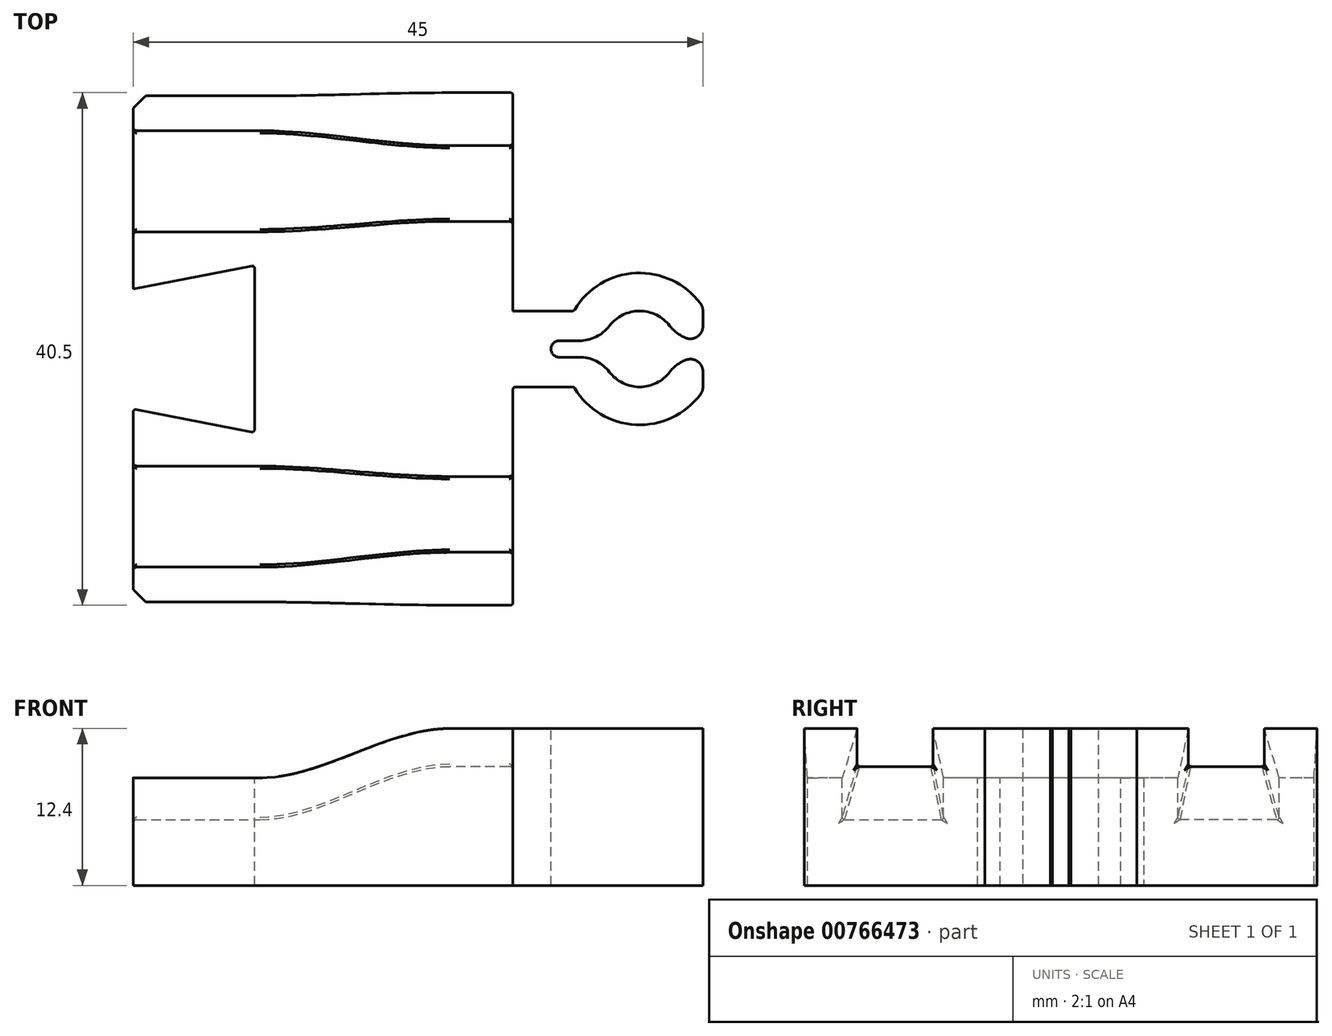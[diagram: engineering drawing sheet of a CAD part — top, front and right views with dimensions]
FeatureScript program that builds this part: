
annotation { "Feature Type Name" : "Feature", "Feature Type Description" : "" }
export const myFeature = defineFeature(function(context is Context, id is Id, definition is map)
    precondition{}
    {
        {
            var Q0;
            Q0=qCreatedBy(makeId("Right.planeOp"),FACE);
            cPlane(context, id + "F0", {"entities" : qUnion([Q0]), "cplaneType" : CPlaneType.OFFSET, "offset" : 15 * mm, "width" : 150 * mm, "height" : 150 * mm});
        }
        {
            var Q0;
            Q0=qCreatedBy(makeId("Right.planeOp"),FACE);
            var sketch = newSketch(context, id + "F1", { "sketchPlane" : qUnion([Q0])});
            skLineSegment(sketch, "E0.bottom", {"start": v(20, 0) * mm, "end": v(-20, 0) * mm});
            skLineSegment(sketch, "E0.top", {"start": v(20, 8.5) * mm, "end": v(17.25, 8.5) * mm});
            skLineSegment(sketch, "E0.left", {"start": v(20, 0) * mm, "end": v(20, 8.5) * mm});
            skLineSegment(sketch, "E0.right", {"start": v(-20, 0) * mm, "end": v(-20, 8.5) * mm});
            skPoint(sketch, "E0.middle", {"position": v(0, 4.25) * mm});
            skLineSegment(sketch, "E1.bottom", {"start": v(17.25, 5.2) * mm, "end": v(9.25, 5.2) * mm});
            skLineSegment(sketch, "E1.left", {"start": v(17.25, 5.2) * mm, "end": v(17.25, 8.5) * mm});
            skLineSegment(sketch, "E1.right", {"start": v(9.25, 5.2) * mm, "end": v(9.25, 8.5) * mm});
            skPoint(sketch, "E1.middle", {"position": v(13.25, 12.03) * mm});
            skPoint(sketch, "E2.orphan", {"position": v(9.25, 18.86) * mm});
            skPoint(sketch, "E3.orphan", {"position": v(17.25, 18.86) * mm});
            skLineSegment(sketch, "E4.trimOffspring", {"start": v(9.25, 8.5) * mm, "end": v(-9.25, 8.5) * mm});
            skLineSegment(sketch, "E5.MirrorCS", {"start": v(-9.25, 5.2) * mm, "end": v(-9.25, 8.5) * mm});
            skLineSegment(sketch, "E6.MirrorCS", {"start": v(-17.25, 5.2) * mm, "end": v(-9.25, 5.2) * mm});
            skLineSegment(sketch, "E7.MirrorCS", {"start": v(-17.25, 5.2) * mm, "end": v(-17.25, 8.5) * mm});
            skLineSegment(sketch, "E8.trimOffspring", {"start": v(-17.25, 8.5) * mm, "end": v(-20, 8.5) * mm});
            skSolve(sketch);
        }
        {
            var Q0;
            Q0=makeQuery(id+"F1.imprint","IMPRINT",FACE,{"disambiguationData":[TD([[makeQuery(id+"F1.imprint","IMPRINT",EDGE,{"derivedFrom":sQuery(id+"F1.wireOp",EDGE,"E0.bottom")}),-1.0]])]});
            extrude(context, id + "F2", {"entities" : qUnion([Q0]), "oppositeDirection" : true, "depth" : 10 * mm, "offsetDistance" : 25 * mm});
        }
        {
            var Q0;
            Q0=qCreatedBy(id+"F0.planeOp",FACE);
            var sketch = newSketch(context, id + "F3", { "sketchPlane" : qUnion([Q0])});
            skLineSegment(sketch, "E9.bottom", {"start": v(20.25, 0) * mm, "end": v(-20.25, 0) * mm});
            skLineSegment(sketch, "E9.top", {"start": v(20.25, 12.4) * mm, "end": v(16.07, 12.4) * mm});
            skLineSegment(sketch, "E9.left", {"start": v(20.25, 0) * mm, "end": v(20.25, 12.4) * mm});
            skLineSegment(sketch, "E9.right", {"start": v(-20.25, 0) * mm, "end": v(-20.25, 12.4) * mm});
            skPoint(sketch, "E9.middle", {"position": v(0, 6.2) * mm});
            skLineSegment(sketch, "E10.bottom", {"start": v(16.07, 9.4) * mm, "end": v(10.07, 9.4) * mm});
            skLineSegment(sketch, "E10.left", {"start": v(16.07, 9.4) * mm, "end": v(16.07, 12.4) * mm});
            skLineSegment(sketch, "E10.right", {"start": v(10.07, 9.4) * mm, "end": v(10.07, 12.4) * mm});
            skPoint(sketch, "E10.middle", {"position": v(13.07, 12.4) * mm});
            skPoint(sketch, "E11.orphan", {"position": v(10.07, 15.41) * mm});
            skLineSegment(sketch, "E12.trimOffspring", {"start": v(10.08, 12.4) * mm, "end": v(-10.08, 12.4) * mm});
            skPoint(sketch, "E13.orphan", {"position": v(16.07, 15.41) * mm});
            skLineSegment(sketch, "E14.MirrorCS", {"start": v(-10.08, 9.4) * mm, "end": v(-10.08, 12.4) * mm});
            skLineSegment(sketch, "E15.MirrorCS", {"start": v(-16.07, 9.4) * mm, "end": v(-10.07, 9.4) * mm});
            skLineSegment(sketch, "E16.MirrorCS", {"start": v(-16.07, 9.4) * mm, "end": v(-16.07, 12.4) * mm});
            skLineSegment(sketch, "E17.trimOffspring", {"start": v(-16.07, 12.4) * mm, "end": v(-20.25, 12.4) * mm});
            skSolve(sketch);
        }
        {
            var Q0;
            Q0=qSketchRegion(id+"F3",true);
            extrude(context, id + "F4", {"entities" : qUnion([Q0]), "depth" : 5 * mm, "offsetDistance" : 25 * mm});
        }
        {
            var Q0;
            Q0=makeQuery(id+"F4.opExtrude","CAP_FACE",FACE,{"disambiguationData":[OSD([sQuery(id+"F3.wireOp",EDGE,"E9.bottom"),sQuery(id+"F3.wireOp",EDGE,"E9.top"),sQuery(id+"F3.wireOp",EDGE,"E9.left"),sQuery(id+"F3.wireOp",EDGE,"E9.right"),sQuery(id+"F3.wireOp",EDGE,"E10.bottom"),sQuery(id+"F3.wireOp",EDGE,"E10.left"),sQuery(id+"F3.wireOp",EDGE,"E10.right"),sQuery(id+"F3.wireOp",EDGE,"E12.trimOffspring"),sQuery(id+"F3.wireOp",EDGE,"E14.MirrorCS"),sQuery(id+"F3.wireOp",EDGE,"E15.MirrorCS"),sQuery(id+"F3.wireOp",EDGE,"E16.MirrorCS"),sQuery(id+"F3.wireOp",EDGE,"E17.trimOffspring")])],"isStart":true});
            var Q1;
            Q1=makeQuery(id+"F2.opExtrude","CAP_FACE",FACE,{"disambiguationData":[OSD([sQuery(id+"F1.wireOp",EDGE,"E0.bottom"),sQuery(id+"F1.wireOp",EDGE,"E0.top"),sQuery(id+"F1.wireOp",EDGE,"E0.left"),sQuery(id+"F1.wireOp",EDGE,"E0.right"),sQuery(id+"F1.wireOp",EDGE,"E1.bottom"),sQuery(id+"F1.wireOp",EDGE,"E1.left"),sQuery(id+"F1.wireOp",EDGE,"E1.right"),sQuery(id+"F1.wireOp",EDGE,"E4.trimOffspring"),sQuery(id+"F1.wireOp",EDGE,"E5.MirrorCS"),sQuery(id+"F1.wireOp",EDGE,"E6.MirrorCS"),sQuery(id+"F1.wireOp",EDGE,"E7.MirrorCS"),sQuery(id+"F1.wireOp",EDGE,"E8.trimOffspring")])],"isStart":true});
            loft(context, id + "F5", {"operationType" : NewBodyOperationType.ADD, "startCondition" : LoftEndDerivativeType.NORMAL_TO_PROFILE, "startMagnitude" : 1, "endCondition" : LoftEndDerivativeType.NORMAL_TO_PROFILE, "endMagnitude" : 1, "sheetProfilesArray" : [{ "sheetProfileEntities" : qUnion([Q0]) }, { "sheetProfileEntities" : qUnion([Q1]) }]});
        }
        {
            var Q0;
            Q0=makeQuery(id+"F2.opExtrude","SWEPT_FACE",FACE,{"disambiguationData":[OSD([sQuery(id+"F1.wireOp",EDGE,"E4.trimOffspring")])]});
            var sketch = newSketch(context, id + "F6", { "sketchPlane" : qUnion([Q0])});
            skLineSegment(sketch, "E18.0", {"start": v(-10, 4.75) * mm, "end": v(-10, -4.75) * mm});
            skLineSegment(sketch, "E19", {"start": v(-10, 4.75) * mm, "end": v(-0.4, 6.6) * mm});
            skLineSegment(sketch, "E20", {"start": v(-0.4, 0) * mm, "end": v(-10, 0) * mm, "construction": true});
            skLineSegment(sketch, "E21.MirrorCS", {"start": v(-10, -4.75) * mm, "end": v(-0.4, -6.6) * mm});
            skLineSegment(sketch, "E22", {"start": v(-0.4, 6.6) * mm, "end": v(-0.4, -6.6) * mm});
            skPoint(sketch, "E23.orphan", {"position": v(-10, 9.25) * mm});
            skPoint(sketch, "E24.orphan", {"position": v(-10, -9.25) * mm});
            skPoint(sketch, "E25.orphan", {"position": v(-32.28, -1.5) * mm});
            skSolve(sketch);
        }
        {
            var Q0;
            Q0=makeQuery(id+"F4.opExtrude","SWEPT_FACE",FACE,{"disambiguationData":[OSD([sQuery(id+"F3.wireOp",EDGE,"E12.trimOffspring")])]});
            var sketch = newSketch(context, id + "F7", { "sketchPlane" : qUnion([Q0])});
            skLineSegment(sketch, "E26.0", {"start": v(20, 10.07) * mm, "end": v(20, -10.08) * mm, "construction": true});
            skLineSegment(sketch, "E27.bottom", {"start": v(20, 3) * mm, "end": v(24.8, 3) * mm});
            skLineSegment(sketch, "E27.top", {"start": v(20, -3) * mm, "end": v(24.8, -3) * mm});
            skLineSegment(sketch, "E27.left", {"start": v(20, 3) * mm, "end": v(20, -3) * mm});
            skPoint(sketch, "E27.middle", {"position": v(23.65, 0) * mm});
            skPoint(sketch, "E27.middle.positionSnap0", {"position": v(20, 0) * mm});
            skPoint(sketch, "E27.centerSnap0", {"position": v(20, 0) * mm});
            skArc(sketch, "E28", {"start": v(35, 3.32) * mm, "mid": v(29.81, 6) * mm, "end": v(24.8, 3) * mm});
            skLineSegment(sketch, "E29", {"start": v(35, 3.32) * mm, "end": v(35, 0.65) * mm});
            skPoint(sketch, "E30.orphan", {"position": v(27.3, 3) * mm});
            skPoint(sketch, "E31.orphan", {"position": v(27.3, -3) * mm});
            skArc(sketch, "E32.trimOffspring", {"start": v(24.8, -3) * mm, "mid": v(29.81, -6) * mm, "end": v(35, -3.32) * mm});
            skLineSegment(sketch, "E33.bottom", {"start": v(23.65, 0.65) * mm, "end": v(27.07, 0.65) * mm});
            skLineSegment(sketch, "E33.top", {"start": v(23.65, -0.65) * mm, "end": v(27.07, -0.65) * mm});
            skArc(sketch, "E34", {"start": v(23.65, 0.65) * mm, "mid": v(23, 0) * mm, "end": v(23.65, -0.65) * mm});
            skPoint(sketch, "E33.left.start.orphan", {"position": v(25, 0.65) * mm});
            skPoint(sketch, "E35.orphan", {"position": v(25, -0.65) * mm});
            skLineSegment(sketch, "E36.trimOffspring", {"start": v(35, -0.65) * mm, "end": v(35, -3.46) * mm});
            skPoint(sketch, "E33.right.end.orphan", {"position": v(35, -0.65) * mm});
            skPoint(sketch, "E33.right.start.orphan", {"position": v(35, 0.65) * mm});
            skArc(sketch, "E37", {"start": v(32.93, 0.65) * mm, "mid": v(30, 3) * mm, "end": v(27.07, 0.65) * mm});
            skLineSegment(sketch, "E38.trimOffspring", {"start": v(32.93, -0.65) * mm, "end": v(35, -0.65) * mm});
            skLineSegment(sketch, "E39.trimOffspring", {"start": v(32.93, 0.65) * mm, "end": v(35, 0.65) * mm});
            skArc(sketch, "E40.trimOffspring", {"start": v(27.07, -0.65) * mm, "mid": v(30, -3) * mm, "end": v(32.93, -0.65) * mm});
            skSolve(sketch);
        }
        {
            var Q0;
            Q0=makeQuery(id+"F7.imprint","IMPRINT",FACE,{"disambiguationData":[TD([[makeQuery(id+"F7.imprint","IMPRINT",EDGE,{"derivedFrom":sQuery(id+"F7.wireOp",EDGE,"E27.bottom")}),-1.0]])]});
            var Q1;
            {var subQ0=sQuery(id+"F3.wireOp",EDGE,"E9.right");var subQ1=sQuery(id+"F3.wireOp",EDGE,"E9.left");var subQ2=sQuery(id+"F3.wireOp",EDGE,"E9.bottom");var subQ3=sQuery(id+"F1.wireOp",EDGE,"E0.right");var subQ4=sQuery(id+"F1.wireOp",EDGE,"E0.left");var subQ5=sQuery(id+"F1.wireOp",EDGE,"E0.bottom");Q1=makeQuery(id+"FUpJ5mfuHsCIaRH_1.boolean.opBoolean","MERGE",FACE,{"derivedFrom":[makeQuery(id+"F5.boolean.opBoolean","MERGE",FACE,{"derivedFrom":[makeQuery(id+"F2.opExtrude","SWEPT_FACE",FACE,{"disambiguationData":[OSD([subQ5])]}),makeQuery(id+"F4.opExtrude","SWEPT_FACE",FACE,{"disambiguationData":[OSD([subQ2])]}),makeQuery(id+"F5.opLoft","SWEPT_FACE",FACE,{"disambiguationData":[OSD([subQ5,subQ4,subQ3,subQ2,subQ1,subQ0])]})]}),makeQuery(id+"FUpJ5mfuHsCIaRH_1.opExtrude","CAP_FACE",FACE,{"disambiguationData":[OSD([subQ5,subQ4,subQ3,subQ2,subQ1,subQ0])],"isStart":false})]});}
            extrude(context, id + "F8", {"entities" : qUnion([Q0]), "operationType" : NewBodyOperationType.ADD, "endBound" : BoundingType.UP_TO_SURFACE, "oppositeDirection" : true, "depth" : 25 * mm, "endBoundEntityFace" : qUnion([Q1]), "offsetDistance" : 25 * mm});
        }
        {
            var Q0;
            Q0=makeQuery(id+"F8.opExtrude","SWEPT_EDGE",EDGE,{"disambiguationData":[OSD([sQuery(id+"F7.wireOp",EDGE,"E33.bottom"),sQuery(id+"F7.wireOp",EDGE,"E37")])]});
            var Q1;
            Q1=makeQuery(id+"F8.opExtrude","SWEPT_EDGE",EDGE,{"disambiguationData":[OSD([sQuery(id+"F7.wireOp",EDGE,"E33.top"),sQuery(id+"F7.wireOp",EDGE,"E40.trimOffspring")])]});
            var Q2;
            Q2=makeQuery(id+"F8.opExtrude","SWEPT_EDGE",EDGE,{"disambiguationData":[OSD([sQuery(id+"F7.wireOp",EDGE,"E37"),sQuery(id+"F7.wireOp",EDGE,"E39.trimOffspring")])]});
            var Q3;
            Q3=makeQuery(id+"F8.opExtrude","SWEPT_EDGE",EDGE,{"disambiguationData":[OSD([sQuery(id+"F7.wireOp",EDGE,"E38.trimOffspring"),sQuery(id+"F7.wireOp",EDGE,"E40.trimOffspring")])]});
            fillet(context, id + "F9", {"entities" : qUnion([Q0, Q1, Q2, Q3]), "radius" : 3 * mm, "tangentPropagation" : true, "allowEdgeOverflow" : false});
        }
        {
            var Q0;
            Q0=makeQuery(id+"F8.opExtrude","SWEPT_EDGE",EDGE,{"disambiguationData":[OSD([sQuery(id+"F7.wireOp",EDGE,"E28"),sQuery(id+"F7.wireOp",EDGE,"E29")])]});
            var Q1;
            Q1=makeQuery(id+"F8.opExtrude","SWEPT_EDGE",EDGE,{"disambiguationData":[OSD([sQuery(id+"F7.wireOp",EDGE,"E29"),sQuery(id+"F7.wireOp",EDGE,"E39.trimOffspring")])]});
            var Q2;
            Q2=makeQuery(id+"F8.opExtrude","SWEPT_EDGE",EDGE,{"disambiguationData":[OSD([sQuery(id+"F7.wireOp",EDGE,"E36.trimOffspring"),sQuery(id+"F7.wireOp",EDGE,"E38.trimOffspring")])]});
            var Q3;
            Q3=makeQuery(id+"F8.opExtrude","SWEPT_EDGE",EDGE,{"disambiguationData":[OSD([sQuery(id+"F7.wireOp",EDGE,"E32.trimOffspring"),sQuery(id+"F7.wireOp",EDGE,"E36.trimOffspring")])]});
            fillet(context, id + "F10", {"entities" : qUnion([Q0, Q1, Q2, Q3]), "radius" : 1 * mm, "tangentPropagation" : true, "allowEdgeOverflow" : false});
        }
        {
            var Q0;
            Q0=makeQuery(id+"F8.opExtrude","SWEPT_EDGE",EDGE,{"disambiguationData":[OSD([sQuery(id+"F3.wireOp",EDGE,"E12.trimOffspring"),sQuery(id+"F7.wireOp",EDGE,"E27.top"),sQuery(id+"F7.wireOp",EDGE,"E27.left")])]});
            var Q1;
            Q1=makeQuery(id+"F8.opExtrude","SWEPT_EDGE",EDGE,{"disambiguationData":[OSD([sQuery(id+"F7.wireOp",EDGE,"E27.top"),sQuery(id+"F7.wireOp",EDGE,"E32.trimOffspring")])]});
            var Q2;
            Q2=makeQuery(id+"F8.opExtrude","SWEPT_EDGE",EDGE,{"disambiguationData":[OSD([sQuery(id+"F3.wireOp",EDGE,"E12.trimOffspring"),sQuery(id+"F7.wireOp",EDGE,"E27.bottom"),sQuery(id+"F7.wireOp",EDGE,"E27.left")])]});
            var Q3;
            Q3=makeQuery(id+"F8.opExtrude","SWEPT_EDGE",EDGE,{"disambiguationData":[OSD([sQuery(id+"F7.wireOp",EDGE,"E27.bottom"),sQuery(id+"F7.wireOp",EDGE,"E28")])]});
            fillet(context, id + "F11", {"entities" : qUnion([Q0, Q1, Q2, Q3]), "radius" : 0.2 * mm, "tangentPropagation" : true, "allowEdgeOverflow" : false});
        }
        {
            var Q0;
            Q0=makeQuery(id+"F2.opExtrude","CAP_EDGE",EDGE,{"disambiguationData":[OSD([sQuery(id+"F1.wireOp",EDGE,"E1.left")])],"isStart":false});
            var Q1;
            Q1=makeQuery(id+"F2.opExtrude","CAP_EDGE",EDGE,{"disambiguationData":[OSD([sQuery(id+"F1.wireOp",EDGE,"E1.right")])],"isStart":false});
            var Q2;
            Q2=makeQuery(id+"F2.opExtrude","CAP_EDGE",EDGE,{"disambiguationData":[OSD([sQuery(id+"F1.wireOp",EDGE,"E1.bottom")])],"isStart":false});
            var Q3;
            Q3=makeQuery(id+"F2.opExtrude","CAP_EDGE",EDGE,{"disambiguationData":[OSD([sQuery(id+"F1.wireOp",EDGE,"E5.MirrorCS")])],"isStart":false});
            var Q4;
            Q4=makeQuery(id+"F2.opExtrude","CAP_EDGE",EDGE,{"disambiguationData":[OSD([sQuery(id+"F1.wireOp",EDGE,"E6.MirrorCS")])],"isStart":false});
            var Q5;
            Q5=makeQuery(id+"F2.opExtrude","CAP_EDGE",EDGE,{"disambiguationData":[OSD([sQuery(id+"F1.wireOp",EDGE,"E7.MirrorCS")])],"isStart":false});
            var Q6;
            Q6=makeQuery(id+"F4.opExtrude","CAP_EDGE",EDGE,{"disambiguationData":[OSD([sQuery(id+"F3.wireOp",EDGE,"E16.MirrorCS")])],"isStart":false});
            var Q7;
            Q7=makeQuery(id+"F4.opExtrude","CAP_EDGE",EDGE,{"disambiguationData":[OSD([sQuery(id+"F3.wireOp",EDGE,"E15.MirrorCS")])],"isStart":false});
            var Q8;
            Q8=makeQuery(id+"F4.opExtrude","CAP_EDGE",EDGE,{"disambiguationData":[OSD([sQuery(id+"F3.wireOp",EDGE,"E14.MirrorCS")])],"isStart":false});
            var Q9;
            Q9=makeQuery(id+"F4.opExtrude","CAP_EDGE",EDGE,{"disambiguationData":[OSD([sQuery(id+"F3.wireOp",EDGE,"E10.left")])],"isStart":false});
            var Q10;
            Q10=makeQuery(id+"F4.opExtrude","CAP_EDGE",EDGE,{"disambiguationData":[OSD([sQuery(id+"F3.wireOp",EDGE,"E10.bottom")])],"isStart":false});
            var Q11;
            Q11=makeQuery(id+"F4.opExtrude","CAP_EDGE",EDGE,{"disambiguationData":[OSD([sQuery(id+"F3.wireOp",EDGE,"E10.right")])],"isStart":false});
            fillet(context, id + "F12", {"entities" : qUnion([Q0, Q1, Q2, Q3, Q4, Q5, Q6, Q7, Q8, Q9, Q10, Q11]), "radius" : 0.3 * mm, "tangentPropagation" : true, "allowEdgeOverflow" : false});
        }
        {
            var Q0;
            Q0=makeQuery(id+"F5.opLoft","SWEPT_EDGE",EDGE,{"disambiguationData":[OSD([sQuery(id+"F1.wireOp",EDGE,"E1.bottom"),sQuery(id+"F1.wireOp",EDGE,"E1.left"),sQuery(id+"F3.wireOp",EDGE,"E10.bottom"),sQuery(id+"F3.wireOp",EDGE,"E10.left")])]});
            var Q1;
            Q1=makeQuery(id+"F5.opLoft","SWEPT_EDGE",EDGE,{"disambiguationData":[OSD([sQuery(id+"F1.wireOp",EDGE,"E1.bottom"),sQuery(id+"F1.wireOp",EDGE,"E1.right"),sQuery(id+"F3.wireOp",EDGE,"E10.bottom"),sQuery(id+"F3.wireOp",EDGE,"E10.right")])]});
            var Q2;
            Q2=makeQuery(id+"F5.opLoft","SWEPT_EDGE",EDGE,{"disambiguationData":[OSD([sQuery(id+"F1.wireOp",EDGE,"E6.MirrorCS"),sQuery(id+"F1.wireOp",EDGE,"E7.MirrorCS"),sQuery(id+"F3.wireOp",EDGE,"E15.MirrorCS"),sQuery(id+"F3.wireOp",EDGE,"E16.MirrorCS")])]});
            var Q3;
            Q3=makeQuery(id+"F5.opLoft","SWEPT_EDGE",EDGE,{"disambiguationData":[OSD([sQuery(id+"F1.wireOp",EDGE,"E5.MirrorCS"),sQuery(id+"F1.wireOp",EDGE,"E6.MirrorCS"),sQuery(id+"F3.wireOp",EDGE,"E14.MirrorCS"),sQuery(id+"F3.wireOp",EDGE,"E15.MirrorCS")])]});
            fillet(context, id + "F13", {"entities" : qUnion([Q0, Q1, Q2, Q3]), "radius" : 0.2 * mm, "tangentPropagation" : true, "allowEdgeOverflow" : false});
        }
        {
            var Q0;
            Q0=makeQuery(id+"F6.imprint","IMPRINT",FACE,{"disambiguationData":[TD([[makeQuery(id+"F6.imprint","IMPRINT",EDGE,{"derivedFrom":sQuery(id+"F6.wireOp",EDGE,"E18.0")}),1.0]])]});
            extrude(context, id + "F14", {"entities" : qUnion([Q0]), "operationType" : NewBodyOperationType.REMOVE, "endBound" : BoundingType.UP_TO_NEXT, "oppositeDirection" : true, "depth" : 25 * mm, "offsetDistance" : 25 * mm});
        }
        {
            var Q0;
            Q0=makeQuery(id+"F14.boolean.opBoolean","COPY",EDGE,{"derivedFrom":makeQuery(id+"F14.opExtrude","SWEPT_EDGE",EDGE,{"disambiguationData":[OSD([sQuery(id+"F1.wireOp",EDGE,"E4.trimOffspring"),sQuery(id+"F6.wireOp",EDGE,"E18.0"),sQuery(id+"F6.wireOp",EDGE,"E19")])]})});
            var Q1;
            Q1=makeQuery(id+"F14.boolean.opBoolean","COPY",EDGE,{"derivedFrom":makeQuery(id+"F14.opExtrude","SWEPT_EDGE",EDGE,{"disambiguationData":[OSD([sQuery(id+"F1.wireOp",EDGE,"E4.trimOffspring"),sQuery(id+"F6.wireOp",EDGE,"E18.0"),sQuery(id+"F6.wireOp",EDGE,"E21.MirrorCS")])]})});
            var Q2;
            Q2=makeQuery(id+"F14.boolean.opBoolean","COPY",EDGE,{"derivedFrom":makeQuery(id+"F14.opExtrude","SWEPT_EDGE",EDGE,{"disambiguationData":[OSD([sQuery(id+"F6.wireOp",EDGE,"E19"),sQuery(id+"F6.wireOp",EDGE,"E22")])]})});
            var Q3;
            Q3=makeQuery(id+"F14.boolean.opBoolean","COPY",EDGE,{"derivedFrom":makeQuery(id+"F14.opExtrude","SWEPT_EDGE",EDGE,{"disambiguationData":[OSD([sQuery(id+"F6.wireOp",EDGE,"E21.MirrorCS"),sQuery(id+"F6.wireOp",EDGE,"E22")])]})});
            fillet(context, id + "F15", {"entities" : qUnion([Q0, Q1, Q2, Q3]), "radius" : 0.2 * mm, "tangentPropagation" : true, "allowEdgeOverflow" : false});
        }
        {
            var Q0;
            Q0=makeQuery(id+"F2.opExtrude","CAP_EDGE",EDGE,{"disambiguationData":[OSD([sQuery(id+"F1.wireOp",EDGE,"E0.left")])],"isStart":false});
            var Q1;
            Q1=makeQuery(id+"F2.opExtrude","CAP_EDGE",EDGE,{"disambiguationData":[OSD([sQuery(id+"F1.wireOp",EDGE,"E0.right")])],"isStart":false});
            chamfer(context, id + "F16", {"entities" : qUnion([Q0, Q1]), "width" : 1 * mm, "tangentPropagation" : true});
        }
        {
            var Q0;
            Q0=makeQuery(id+"F4.opExtrude","CAP_EDGE",EDGE,{"disambiguationData":[OSD([sQuery(id+"F3.wireOp",EDGE,"E9.left")])],"isStart":false});
            var Q1;
            {var subQ0=sQuery(id+"F1.wireOp",EDGE,"E0.left");Q1=makeQuery(id+"F16.opChamfer","BLEND_EDGE",EDGE,{"blendedFrom":[makeQuery(id+"F2.opExtrude","CAP_EDGE",EDGE,{"disambiguationData":[OSD([subQ0])],"isStart":false}),makeQuery(id+"F2.opExtrude","SWEPT_FACE",FACE,{"disambiguationData":[OSD([subQ0])]})],"blendedInto":[makeQuery(id+"F2.opExtrude","SWEPT_FACE",FACE,{"disambiguationData":[OSD([subQ0])]})]});}
            var Q2;
            {var subQ0=sQuery(id+"F1.wireOp",EDGE,"E7.MirrorCS");var subQ1=sQuery(id+"F1.wireOp",EDGE,"E5.MirrorCS");var subQ2=sQuery(id+"F1.wireOp",EDGE,"E0.bottom");var subQ6=sQuery(id+"F1.wireOp",EDGE,"E0.right");var subQ7=sQuery(id+"F1.wireOp",EDGE,"E0.left");var subQ8=sQuery(id+"F1.wireOp",EDGE,"E8.trimOffspring");var subQ9=sQuery(id+"F1.wireOp",EDGE,"E6.MirrorCS");var subQ10=sQuery(id+"F1.wireOp",EDGE,"E4.trimOffspring");Q2=makeQuery(id+"F16.opChamfer","BLEND_EDGE",EDGE,{"blendedFrom":[makeQuery(id+"F2.opExtrude","CAP_EDGE",EDGE,{"disambiguationData":[OSD([subQ6])],"isStart":false}),makeQuery(id+"F14.boolean.opBoolean","SPLIT",FACE,{"disambiguationData":[TD([makeQuery(id+"F2.opExtrude","SWEPT_FACE",FACE,{"disambiguationData":[OSD([subQ6])]})])],"derivedFrom":makeQuery(id+"F2.opExtrude","CAP_FACE",FACE,{"disambiguationData":[OSD([subQ2,sQuery(id+"F1.wireOp",EDGE,"E0.top"),subQ7,subQ6,sQuery(id+"F1.wireOp",EDGE,"E1.bottom"),sQuery(id+"F1.wireOp",EDGE,"E1.left"),sQuery(id+"F1.wireOp",EDGE,"E1.right"),subQ10,subQ1,subQ9,subQ0,subQ8])],"isStart":false})})],"blendedInto":[makeQuery(id+"F14.boolean.opBoolean","SPLIT",FACE,{"disambiguationData":[TD([makeQuery(id+"F2.opExtrude","SWEPT_FACE",FACE,{"disambiguationData":[OSD([subQ6])]})])],"derivedFrom":makeQuery(id+"F2.opExtrude","CAP_FACE",FACE,{"disambiguationData":[OSD([subQ2,sQuery(id+"F1.wireOp",EDGE,"E0.top"),subQ7,subQ6,sQuery(id+"F1.wireOp",EDGE,"E1.bottom"),sQuery(id+"F1.wireOp",EDGE,"E1.left"),sQuery(id+"F1.wireOp",EDGE,"E1.right"),subQ10,subQ1,subQ9,subQ0,subQ8])],"isStart":false})})]});}
            var Q3;
            {var subQ0=sQuery(id+"F1.wireOp",EDGE,"E0.right");Q3=makeQuery(id+"F16.opChamfer","BLEND_EDGE",EDGE,{"blendedFrom":[makeQuery(id+"F2.opExtrude","CAP_EDGE",EDGE,{"disambiguationData":[OSD([subQ0])],"isStart":false}),makeQuery(id+"F2.opExtrude","SWEPT_FACE",FACE,{"disambiguationData":[OSD([subQ0])]})],"blendedInto":[makeQuery(id+"F2.opExtrude","SWEPT_FACE",FACE,{"disambiguationData":[OSD([subQ0])]})]});}
            var Q4;
            Q4=makeQuery(id+"F4.opExtrude","CAP_EDGE",EDGE,{"disambiguationData":[OSD([sQuery(id+"F3.wireOp",EDGE,"E9.right")])],"isStart":false});
            var Q5;
            {var subQ0=sQuery(id+"F1.wireOp",EDGE,"E1.left");var subQ4=sQuery(id+"F1.wireOp",EDGE,"E0.right");var subQ5=sQuery(id+"F1.wireOp",EDGE,"E0.left");var subQ6=sQuery(id+"F1.wireOp",EDGE,"E0.bottom");var subQ7=sQuery(id+"F1.wireOp",EDGE,"E1.right");var subQ8=sQuery(id+"F1.wireOp",EDGE,"E1.bottom");var subQ9=sQuery(id+"F1.wireOp",EDGE,"E0.top");var subQ10=sQuery(id+"F1.wireOp",EDGE,"E4.trimOffspring");Q5=makeQuery(id+"F16.opChamfer","BLEND_EDGE",EDGE,{"blendedFrom":[makeQuery(id+"F2.opExtrude","CAP_EDGE",EDGE,{"disambiguationData":[OSD([subQ5])],"isStart":false}),makeQuery(id+"F14.boolean.opBoolean","SPLIT",FACE,{"disambiguationData":[TD([makeQuery(id+"F2.opExtrude","SWEPT_FACE",FACE,{"disambiguationData":[OSD([subQ9])]})])],"derivedFrom":makeQuery(id+"F2.opExtrude","CAP_FACE",FACE,{"disambiguationData":[OSD([subQ6,subQ9,subQ5,subQ4,subQ8,subQ0,subQ7,subQ10,sQuery(id+"F1.wireOp",EDGE,"E5.MirrorCS"),sQuery(id+"F1.wireOp",EDGE,"E6.MirrorCS"),sQuery(id+"F1.wireOp",EDGE,"E7.MirrorCS"),sQuery(id+"F1.wireOp",EDGE,"E8.trimOffspring")])],"isStart":false})})],"blendedInto":[makeQuery(id+"F14.boolean.opBoolean","SPLIT",FACE,{"disambiguationData":[TD([makeQuery(id+"F2.opExtrude","SWEPT_FACE",FACE,{"disambiguationData":[OSD([subQ9])]})])],"derivedFrom":makeQuery(id+"F2.opExtrude","CAP_FACE",FACE,{"disambiguationData":[OSD([subQ6,subQ9,subQ5,subQ4,subQ8,subQ0,subQ7,subQ10,sQuery(id+"F1.wireOp",EDGE,"E5.MirrorCS"),sQuery(id+"F1.wireOp",EDGE,"E6.MirrorCS"),sQuery(id+"F1.wireOp",EDGE,"E7.MirrorCS"),sQuery(id+"F1.wireOp",EDGE,"E8.trimOffspring")])],"isStart":false})})]});}
            fillet(context, id + "F17", {"entities" : qUnion([Q0, Q1, Q2, Q3, Q4, Q5]), "radius" : 0.2 * mm, "tangentPropagation" : true, "allowEdgeOverflow" : false});
        }
    });
